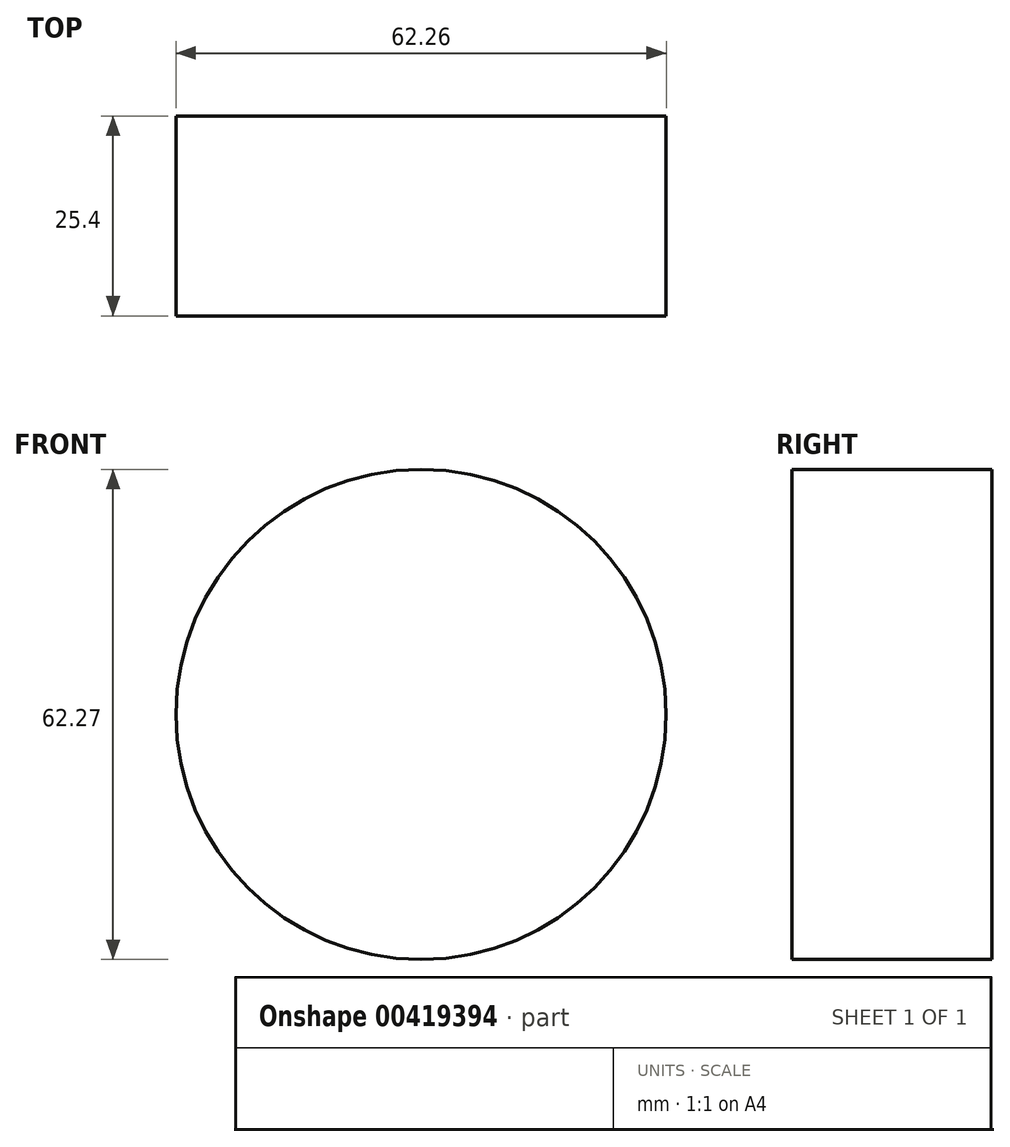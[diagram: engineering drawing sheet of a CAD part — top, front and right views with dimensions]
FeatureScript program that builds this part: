
annotation { "Feature Type Name" : "Feature", "Feature Type Description" : "" }
export const myFeature = defineFeature(function(context is Context, id is Id, definition is map)
    precondition{}
    {
        {
            var Q0;
            Q0=qCreatedBy(makeId("Front.planeOp"),FACE);
            var sketch = newSketch(context, id + "F0", { "sketchPlane" : qUnion([Q0])});
            skCircle(sketch, "E0", {"center": v(-30.36, 43.16) * mm, "radius": 31.13 * mm});
            skSolve(sketch);
        }
        {
            var Q0;
            Q0 = qSketchRegion(id + "F0", true);
            extrude(context, id + "F1", {"entities" : qUnion([Q0]), "depth" : 25.4 * mm});
        }
    });
